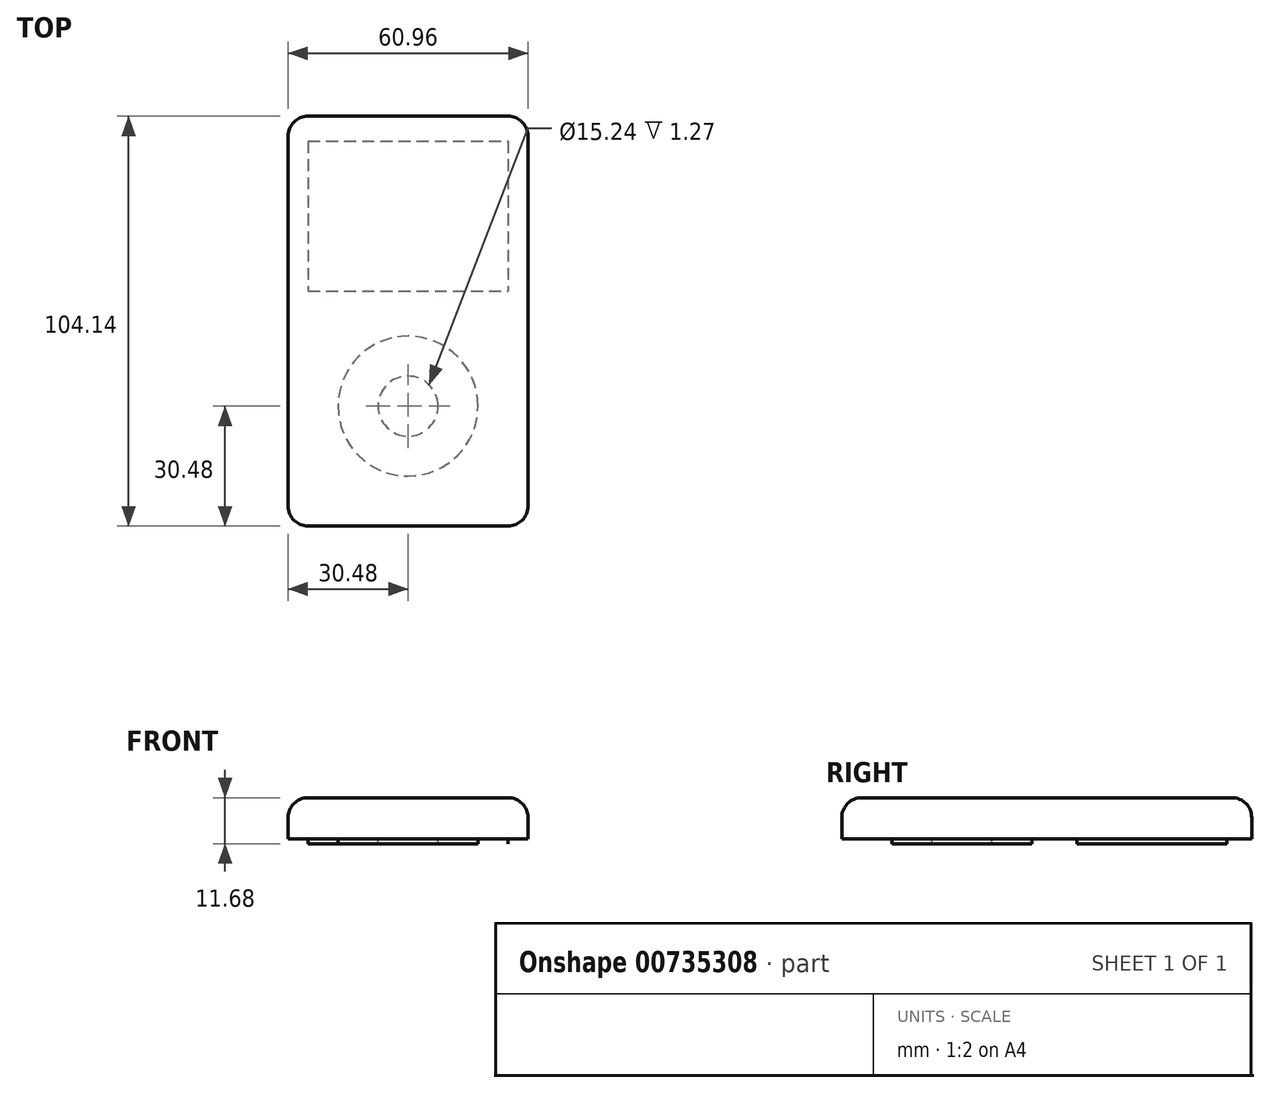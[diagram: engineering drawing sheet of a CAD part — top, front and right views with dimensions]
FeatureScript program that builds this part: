
annotation { "Feature Type Name" : "Feature", "Feature Type Description" : "" }
export const myFeature = defineFeature(function(context is Context, id is Id, definition is map)
    precondition{}
    {
        {
            var Q0;
            Q0=qCreatedBy(makeId("Top.planeOp"),FACE);
            var sketch = newSketch(context, id + "F0", { "sketchPlane" : qUnion([Q0])});
            skLineSegment(sketch, "E0.bottom", {"start": v(-25.4, 52.07) * mm, "end": v(25.4, 52.07) * mm});
            skLineSegment(sketch, "E0.top", {"start": v(-25.4, -52.07) * mm, "end": v(25.4, -52.07) * mm});
            skLineSegment(sketch, "E0.left", {"start": v(-30.48, 46.99) * mm, "end": v(-30.48, -46.99) * mm});
            skLineSegment(sketch, "E0.right", {"start": v(30.48, 46.99) * mm, "end": v(30.48, -46.99) * mm});
            skPoint(sketch, "E0.middle", {"position": v(0, 0) * mm});
            skLineSegment(sketch, "E1.bottom", {"start": v(-25.4, 45.72) * mm, "end": v(25.4, 45.72) * mm});
            skLineSegment(sketch, "E1.top", {"start": v(-25.4, 7.62) * mm, "end": v(25.4, 7.62) * mm});
            skLineSegment(sketch, "E1.left", {"start": v(-25.4, 45.72) * mm, "end": v(-25.4, 7.62) * mm});
            skLineSegment(sketch, "E1.right", {"start": v(25.4, 45.72) * mm, "end": v(25.4, 7.62) * mm});
            skPoint(sketch, "E1.middle", {"position": v(0, 26.67) * mm});
            skCircle(sketch, "E2", {"center": v(0, -21.59) * mm, "radius": 17.78 * mm});
            skCircle(sketch, "E3", {"center": v(0, -21.59) * mm, "radius": 7.62 * mm});
            skPoint(sketch, "E4.visualSharp", {"position": v(30.48, 52.07) * mm});
            skArc(sketch, "E4.filletArc", {"start": v(30.48, 46.99) * mm, "mid": v(29, 50.58) * mm, "end": v(25.4, 52.07) * mm});
            skPoint(sketch, "E5.visualSharp", {"position": v(-30.48, 52.07) * mm});
            skArc(sketch, "E5.filletArc", {"start": v(-25.4, 52.07) * mm, "mid": v(-29, 50.58) * mm, "end": v(-30.48, 46.99) * mm});
            skPoint(sketch, "E6.visualSharp", {"position": v(-30.48, -52.07) * mm});
            skArc(sketch, "E6.filletArc", {"start": v(-30.48, -46.99) * mm, "mid": v(-29, -50.58) * mm, "end": v(-25.4, -52.07) * mm});
            skPoint(sketch, "E7.visualSharp", {"position": v(30.48, -52.07) * mm});
            skArc(sketch, "E7.filletArc", {"start": v(25.4, -52.07) * mm, "mid": v(29, -50.58) * mm, "end": v(30.48, -46.99) * mm});
            skSolve(sketch);
        }
        {
            var Q0;
            Q0=makeQuery(id+"F0.imprint","IMPRINT",FACE,{"disambiguationData":[TD([[makeQuery(id+"F0.imprint","IMPRINT",EDGE,{"derivedFrom":sQuery(id+"F0.wireOp",EDGE,"E0.bottom")}),-1.0]])]});
            var Q1;
            Q1=makeQuery(id+"F0.imprint","IMPRINT",FACE,{"disambiguationData":[TD([[makeQuery(id+"F0.imprint","IMPRINT",EDGE,{"derivedFrom":sQuery(id+"F0.wireOp",EDGE,"E1.bottom")}),-1.0]])]});
            var Q2;
            Q2=makeQuery(id+"F0.imprint","IMPRINT",FACE,{"disambiguationData":[TD([[makeQuery(id+"F0.imprint","IMPRINT",EDGE,{"derivedFrom":sQuery(id+"F0.wireOp",EDGE,"E3")}),1.0]])]});
            var Q3;
            Q3=makeQuery(id+"F0.imprint","IMPRINT",FACE,{"disambiguationData":[TD([[makeQuery(id+"F0.imprint","IMPRINT",EDGE,{"derivedFrom":sQuery(id+"F0.wireOp",EDGE,"E2")}),1.0]])]});
            extrude(context, id + "F1", {"entities" : qUnion([Q0, Q1, Q2, Q3]), "depth" : 10.4 * mm, "offsetDistance" : 25.4 * mm});
        }
        {
            var Q0;
            Q0=makeQuery(id+"F0.imprint","IMPRINT",FACE,{"disambiguationData":[TD([[makeQuery(id+"F0.imprint","IMPRINT",EDGE,{"derivedFrom":sQuery(id+"F0.wireOp",EDGE,"E2")}),1.0]])]});
            var Q1;
            Q1=makeQuery(id+"F0.imprint","IMPRINT",FACE,{"disambiguationData":[TD([[makeQuery(id+"F0.imprint","IMPRINT",EDGE,{"derivedFrom":sQuery(id+"F0.wireOp",EDGE,"E1.bottom")}),-1.0]])]});
            extrude(context, id + "F2", {"entities" : qUnion([Q0, Q1]), "operationType" : NewBodyOperationType.ADD, "oppositeDirection" : true, "depth" : 1.27 * mm, "offsetDistance" : 25.4 * mm});
        }
        {
            var Q0;
            Q0=makeQuery(id+"F1.opExtrude","CAP_EDGE",EDGE,{"disambiguationData":[OSD([sQuery(id+"F0.wireOp",EDGE,"E0.top")])],"isStart":false});
            var Q1;
            Q1=makeQuery(id+"F1.opExtrude","CAP_EDGE",EDGE,{"disambiguationData":[OSD([sQuery(id+"F0.wireOp",EDGE,"E0.bottom")])],"isStart":false});
            fillet(context, id + "F3", {"entities" : qUnion([Q0, Q1]), "radius" : 5.08 * mm, "tangentPropagation" : true, "allowEdgeOverflow" : false});
        }
    });
